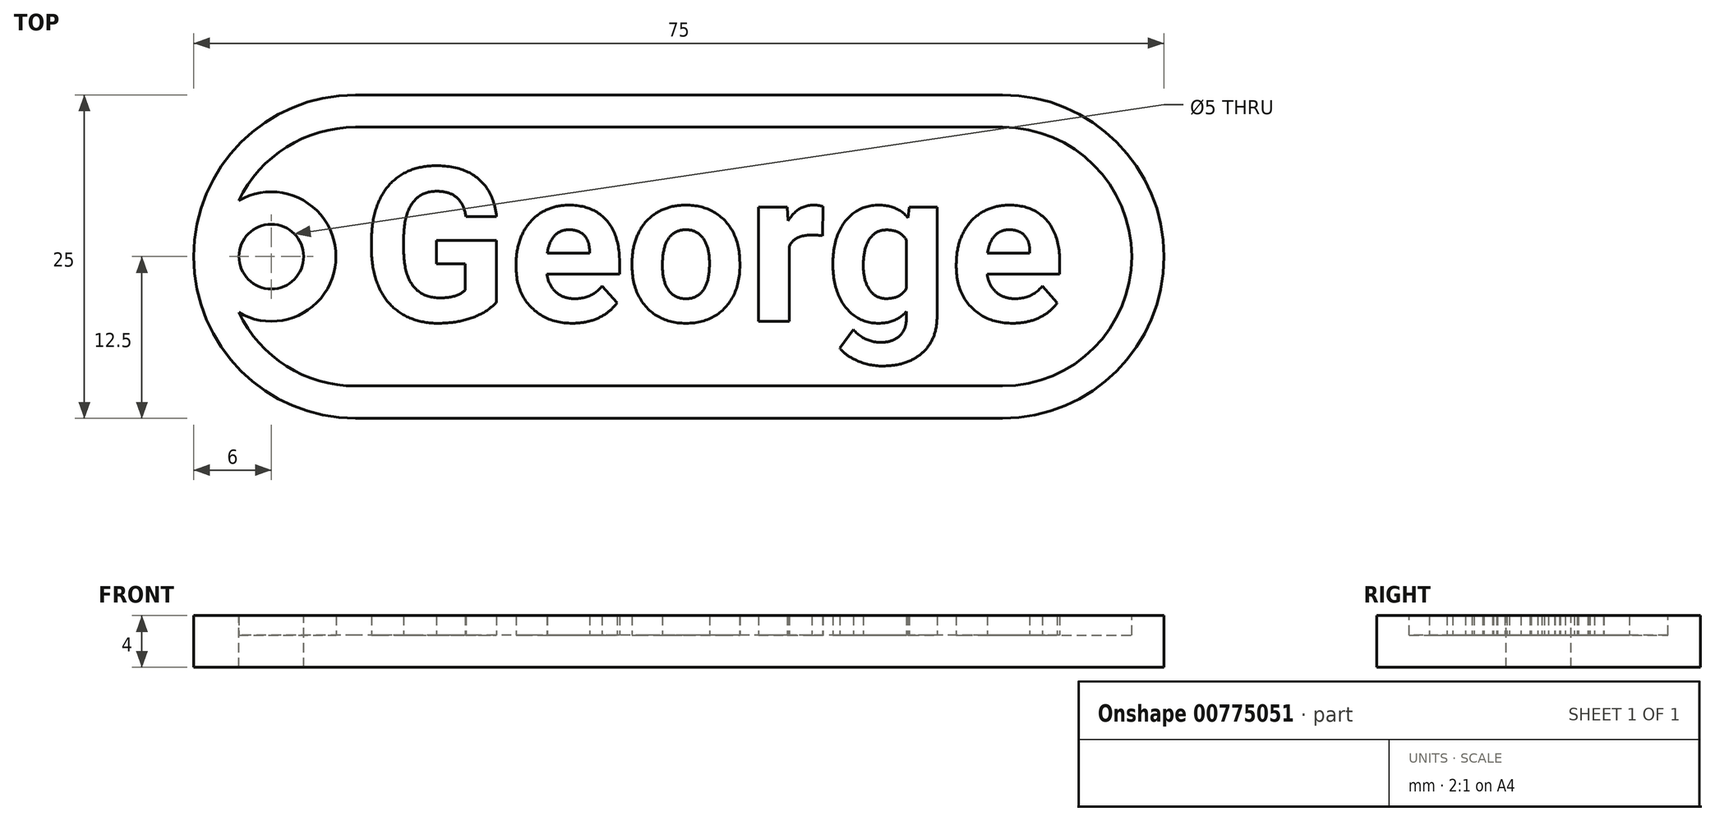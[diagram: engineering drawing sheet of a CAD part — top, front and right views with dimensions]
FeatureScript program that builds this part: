
annotation { "Feature Type Name" : "Feature", "Feature Type Description" : "" }
export const myFeature = defineFeature(function(context is Context, id is Id, definition is map)
    precondition{}
    {
        {
            var Q0;
            Q0=qCreatedBy(makeId("Top.planeOp"),FACE);
            var sketch = newSketch(context, id + "F0", { "sketchPlane" : qUnion([Q0]), "disableImprinting" : false});
            skLineSegment(sketch, "E0.bottom", {"start": v(12.5, 0) * mm, "end": v(62.5, 0) * mm});
            skLineSegment(sketch, "E0.top", {"start": v(12.5, 25) * mm, "end": v(62.5, 25) * mm});
            skArc(sketch, "E1", {"start": v(12.5, 25) * mm, "mid": v(0, 12.5) * mm, "end": v(12.5, 0) * mm});
            skPoint(sketch, "E1.centerSnap0", {"position": v(0, 12.5) * mm});
            skArc(sketch, "E2", {"start": v(62.5, 0) * mm, "mid": v(75, 12.5) * mm, "end": v(62.5, 25) * mm});
            skPoint(sketch, "E2.centerSnap0", {"position": v(75, 12.5) * mm});
            skPoint(sketch, "E3.orphan", {"position": v(0, 25) * mm});
            skPoint(sketch, "E4.orphan", {"position": v(0, 0) * mm});
            skPoint(sketch, "E5.orphan", {"position": v(75, 25) * mm});
            skPoint(sketch, "E6.orphan", {"position": v(75, 0) * mm});
            skSolve(sketch);
        }
        {
            var Q0;
            Q0=makeQuery(id+"F0.imprint","IMPRINT",FACE,{"disambiguationData":[TD([[makeQuery(id+"F0.imprint","IMPRINT",EDGE,{"derivedFrom":sQuery(id+"F0.wireOp",EDGE,"E0.bottom")}),1.0]])]});
            extrude(context, id + "F1", {"entities" : qUnion([Q0]), "depth" : 4 * mm, "offsetDistance" : 25 * mm});
        }
        {
            var Q0;
            Q0=makeQuery(id+"F1.opExtrude","CAP_FACE",FACE,{"disambiguationData":[OSD([sQuery(id+"F0.wireOp",EDGE,"E0.bottom"),sQuery(id+"F0.wireOp",EDGE,"E0.top"),sQuery(id+"F0.wireOp",EDGE,"E1"),sQuery(id+"F0.wireOp",EDGE,"E2")])],"isStart":false});
            var sketch = newSketch(context, id + "F2", { "sketchPlane" : qUnion([Q0])});
            skArc(sketch, "E7", {"start": v(12.5, 22.5) * mm, "mid": v(2.5, 12.5) * mm, "end": v(12.5, 2.5) * mm});
            skArc(sketch, "E8", {"start": v(62.5, 2.5) * mm, "mid": v(72.5, 12.5) * mm, "end": v(62.5, 22.5) * mm});
            skLineSegment(sketch, "E9", {"start": v(12.5, 22.5) * mm, "end": v(62.5, 22.5) * mm});
            skLineSegment(sketch, "E10", {"start": v(62.5, 2.5) * mm, "end": v(12.5, 2.5) * mm});
            skSolve(sketch);
        }
        {
            var Q0;
            Q0=makeQuery(id+"F2.imprint","IMPRINT",FACE,{"disambiguationData":[TD([[makeQuery(id+"F2.imprint","IMPRINT",EDGE,{"derivedFrom":sQuery(id+"F2.wireOp",EDGE,"E7")}),1.0]])]});
            extrude(context, id + "F3", {"entities" : qUnion([Q0]), "operationType" : NewBodyOperationType.REMOVE, "oppositeDirection" : true, "depth" : 1.5 * mm, "offsetDistance" : 25 * mm});
        }
        {
            var Q0;
            Q0=makeQuery(id+"F3.boolean.opBoolean","COPY",FACE,{"derivedFrom":makeQuery(id+"F3.opExtrude","CAP_FACE",FACE,{"disambiguationData":[OSD([sQuery(id+"F2.wireOp",EDGE,"E7"),sQuery(id+"F2.wireOp",EDGE,"E8"),sQuery(id+"F2.wireOp",EDGE,"E9"),sQuery(id+"F2.wireOp",EDGE,"E10")])],"isStart":false})});
            var sketch = newSketch(context, id + "F4", { "sketchPlane" : qUnion([Q0])});
            skCircle(sketch, "E11", {"center": v(6, 12.5) * mm, "radius": 5 * mm});
            skPoint(sketch, "E11.centerSnap0", {"position": v(2.5, 12.5) * mm});
            skSolve(sketch);
        }
        {
            var Q0;
            {var subQ0=sQuery(id+"F4.wireOp",EDGE,"E11");var subQ1=makeQuery(id+"F3.boolean.opBoolean","COPY",EDGE,{"derivedFrom":makeQuery(id+"F3.opExtrude","CAP_EDGE",EDGE,{"disambiguationData":[OSD([sQuery(id+"F2.wireOp",EDGE,"E7")])],"isStart":false})});var subQ2=makeQuery(id+"F4.imprint","INTERSECT",VERTEX,{"disambiguationData":[OD(0.0)],"derivedFrom":[subQ1,subQ0]});Q0=makeQuery(id+"F4.imprint","IMPRINT",FACE,{"disambiguationData":[TD([[makeQuery(id+"F4.imprint","IMPRINT",EDGE,{"disambiguationData":[TD([[subQ2,1.0]])],"derivedFrom":subQ0}),1.0]])]});}
            extrude(context, id + "F5", {"entities" : qUnion([Q0]), "operationType" : NewBodyOperationType.ADD, "depth" : 1.5 * mm, "offsetDistance" : 25 * mm});
        }
        {
            var Q0;
            Q0=makeQuery(id+"F5.boolean.opBoolean","MERGE",FACE,{"derivedFrom":[makeQuery(id+"F1.opExtrude","CAP_FACE",FACE,{"disambiguationData":[OSD([sQuery(id+"F0.wireOp",EDGE,"E0.bottom"),sQuery(id+"F0.wireOp",EDGE,"E0.top"),sQuery(id+"F0.wireOp",EDGE,"E1"),sQuery(id+"F0.wireOp",EDGE,"E2")])],"isStart":false}),makeQuery(id+"F5.opExtrude","CAP_FACE",FACE,{"disambiguationData":[OSD([sQuery(id+"F2.wireOp",EDGE,"E7"),sQuery(id+"F4.wireOp",EDGE,"E11")])],"isStart":false})]});
            var sketch = newSketch(context, id + "F6", { "sketchPlane" : qUnion([Q0])});
            skCircle(sketch, "E12", {"center": v(6, 12.5) * mm, "radius": 2.5 * mm});
            skSolve(sketch);
        }
        {
            var Q0;
            Q0=makeQuery(id+"F6.imprint","IMPRINT",FACE,{"disambiguationData":[TD([[makeQuery(id+"F6.imprint","IMPRINT",EDGE,{"derivedFrom":sQuery(id+"F6.wireOp",EDGE,"E12")}),1.0]])]});
            extrude(context, id + "F7", {"entities" : qUnion([Q0]), "operationType" : NewBodyOperationType.REMOVE, "oppositeDirection" : true, "depth" : 25 * mm, "offsetDistance" : 25 * mm});
        }
        {
            var Q0;
            Q0=makeQuery(id+"F3.boolean.opBoolean","COPY",FACE,{"derivedFrom":makeQuery(id+"F3.opExtrude","CAP_FACE",FACE,{"disambiguationData":[OSD([sQuery(id+"F2.wireOp",EDGE,"E7"),sQuery(id+"F2.wireOp",EDGE,"E8"),sQuery(id+"F2.wireOp",EDGE,"E9"),sQuery(id+"F2.wireOp",EDGE,"E10")])],"isStart":false})});
            var sketch = newSketch(context, id + "F8", { "sketchPlane" : qUnion([Q0]), "disableImprinting" : false});
            skText(sketch, "E13", { "text": "George", "fontName": "Roboto-Bold.ttf"});
            const initialGuessF8  = {"E13": [0.01298, 0.00751, 1, 0, 0.012]};
            skSetInitialGuess(sketch, initialGuessF8);
            skSolve(sketch);
        }
        {
            var Q0;
            Q0 = qSketchRegion(id + "F8", true);
            extrude(context, id + "F9", {"entities" : qUnion([Q0]), "operationType" : NewBodyOperationType.ADD, "depth" : 1.5 * mm, "offsetDistance" : 25 * mm});
        }
    });
